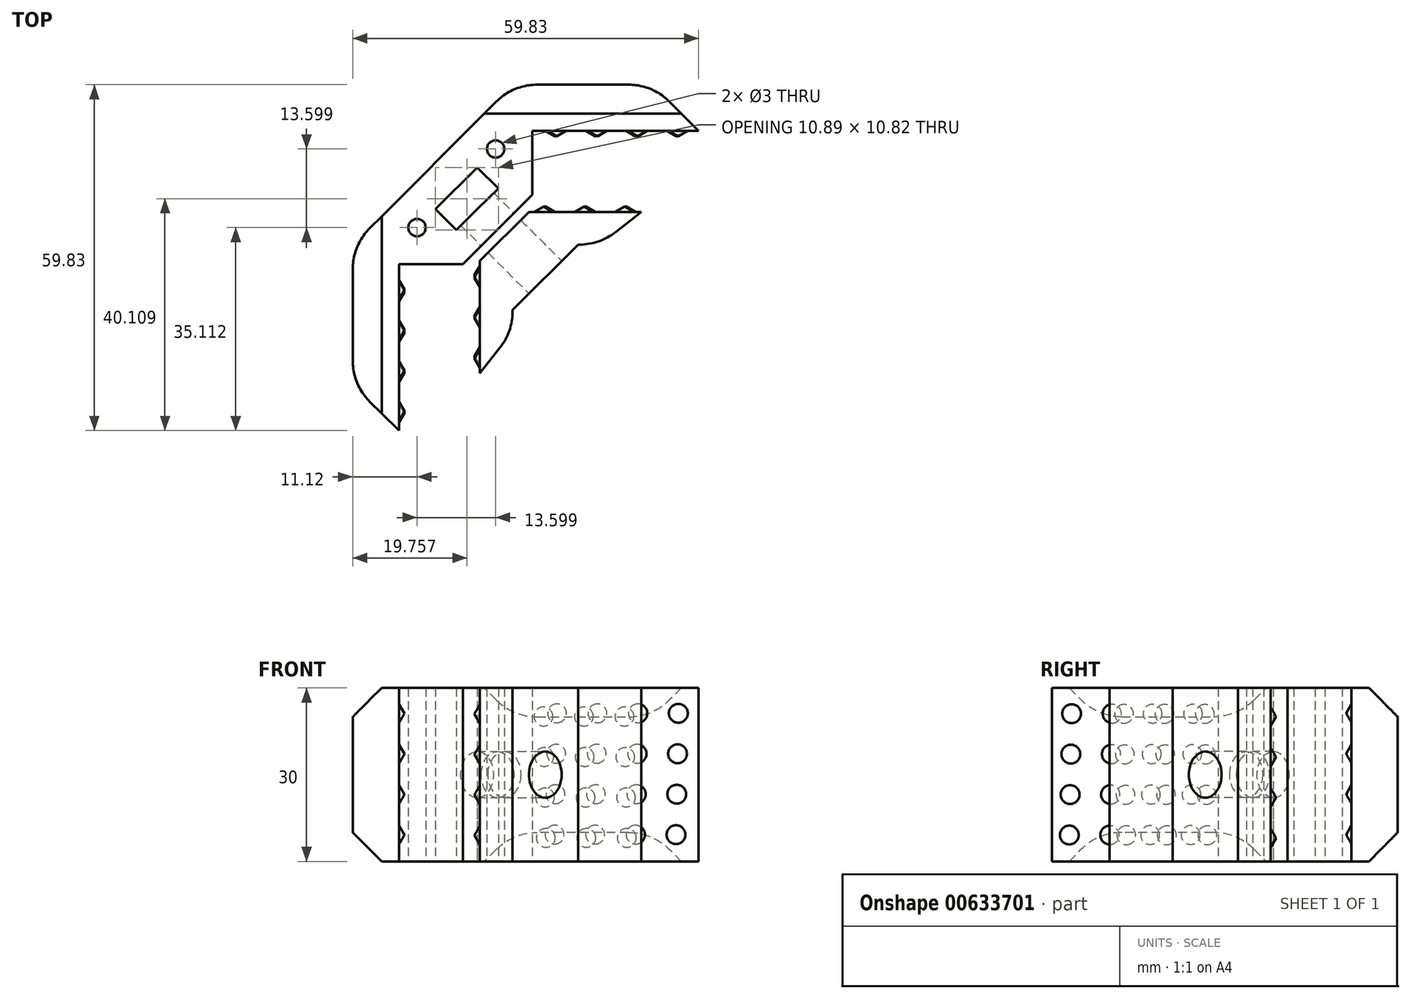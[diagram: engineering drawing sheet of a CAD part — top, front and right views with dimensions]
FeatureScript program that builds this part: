
annotation { "Feature Type Name" : "Feature", "Feature Type Description" : "" }
export const myFeature = defineFeature(function(context is Context, id is Id, definition is map)
    precondition{}
    {
        {
            var Q0;
            Q0=qCreatedBy(makeId("Top.planeOp"),FACE);
            var sketch = newSketch(context, id + "F0", { "sketchPlane" : qUnion([Q0])});
            skLineSegment(sketch, "E0.bottom", {"start": v(0, 0) * mm, "end": v(11.05, 0) * mm});
            skLineSegment(sketch, "E0.left", {"start": v(0, 0) * mm, "end": v(0, -28.76) * mm});
            skLineSegment(sketch, "E0.right", {"start": v(16, -1.41) * mm, "end": v(16, -20.83) * mm});
            skLineSegment(sketch, "E1", {"start": v(23.07, 12.02) * mm, "end": v(23.07, 23.07) * mm});
            skLineSegment(sketch, "E2", {"start": v(23.07, 23.07) * mm, "end": v(51.83, 23.07) * mm});
            skLineSegment(sketch, "E3", {"start": v(24.49, 7.07) * mm, "end": v(43.9, 7.07) * mm});
            skLineSegment(sketch, "E4", {"start": v(0, 0) * mm, "end": v(23.07, 23.07) * mm, "construction": true});
            skLineSegment(sketch, "E5.0", {"start": v(-8, 3.31) * mm, "end": v(-8, -20.83) * mm});
            skLineSegment(sketch, "E5.1", {"start": v(-8, 3.31) * mm, "end": v(19.76, 31.07) * mm});
            skLineSegment(sketch, "E5.2", {"start": v(19.76, 31.07) * mm, "end": v(43.9, 31.07) * mm});
            skLineSegment(sketch, "E6", {"start": v(21.66, -5.66) * mm, "end": v(21.66, -13.66) * mm});
            skLineSegment(sketch, "E7.MirrorCS", {"start": v(28.73, 1.41) * mm, "end": v(36.73, 1.41) * mm});
            skLineSegment(sketch, "E8", {"start": v(21.66, -13.66) * mm, "end": v(16, -20.83) * mm});
            skLineSegment(sketch, "E9", {"start": v(-8, -20.83) * mm, "end": v(0, -28.76) * mm});
            skLineSegment(sketch, "E10.MirrorCS", {"start": v(36.73, 1.41) * mm, "end": v(43.9, 7.07) * mm});
            skLineSegment(sketch, "E11.MirrorCS", {"start": v(43.9, 31.07) * mm, "end": v(51.83, 23.07) * mm});
            skLineSegment(sketch, "E12", {"start": v(9.92, 5.94) * mm, "end": v(6.31, 9.55) * mm});
            skLineSegment(sketch, "E13", {"start": v(6.31, 9.55) * mm, "end": v(13.53, 16.76) * mm});
            skLineSegment(sketch, "E14", {"start": v(13.53, 16.76) * mm, "end": v(17.2, 13.08) * mm});
            skLineSegment(sketch, "E15", {"start": v(17.2, 13.08) * mm, "end": v(13.53, 9.55) * mm});
            skCircle(sketch, "E16", {"center": v(3.12, 6.35) * mm, "radius": 1.5 * mm});
            skLineSegment(sketch, "E17", {"start": v(9.92, 5.94) * mm, "end": v(13.53, 9.55) * mm});
            skCircle(sketch, "E18.MirrorC", {"center": v(16.72, 19.95) * mm, "radius": 1.5 * mm});
            skPoint(sketch, "E19.end.orphan", {"position": v(123.07, 23.07) * mm});
            skPoint(sketch, "E19.start.orphan", {"position": v(123.07, 7.07) * mm});
            skLineSegment(sketch, "E20.0", {"start": v(21.66, -9.9) * mm, "end": v(32.97, 1.41) * mm});
            skLineSegment(sketch, "E21.0", {"start": v(16, -1.41) * mm, "end": v(24.49, 7.07) * mm});
            skLineSegment(sketch, "E22.0", {"start": v(11.05, 0) * mm, "end": v(23.07, 12.02) * mm});
            skPoint(sketch, "E23.orphan", {"position": v(23.07, 7.07) * mm});
            skSolve(sketch);
        }
        {
            var Q0;
            {var subQ7=sQuery(id+"F0.wireOp",EDGE,"E0.bottom");Q0=makeQuery(id+"F0.imprint","IMPRINT",FACE,{"disambiguationData":[TD([[makeQuery(id+"F0.imprint","IMPRINT",EDGE,{"derivedFrom":subQ7}),1.0]])]});}
            extrude(context, id + "F1", {"entities" : qUnion([Q0]), "depth" : 30 * mm, "offsetDistance" : 25 * mm});
        }
        {
            var Q0;
            Q0=makeQuery(id+"F0.imprint","IMPRINT",FACE,{"disambiguationData":[TD([[makeQuery(id+"F0.imprint","IMPRINT",EDGE,{"derivedFrom":sQuery(id+"F0.wireOp",EDGE,"E0.right")}),1.0]])]});
            extrude(context, id + "F2", {"entities" : qUnion([Q0]), "depth" : 30 * mm, "offsetDistance" : 25 * mm});
        }
        {
            var Q0;
            Q0=makeQuery(id+"F2.opExtrude","SWEPT_FACE",FACE,{"disambiguationData":[OSD([sQuery(id+"F0.wireOp",EDGE,"E20.0")])]});
            var sketch = newSketch(context, id + "F3", { "sketchPlane" : qUnion([Q0])});
            skPoint(sketch, "E24", {"position": v(16.31, 15) * mm});
            skPoint(sketch, "E24.positionSnap0", {"position": v(11.31, 15) * mm});
            skPoint(sketch, "E24.positionSnap1", {"position": v(16.31, 30) * mm});
            skCircle(sketch, "E25", {"center": v(16.31, 15) * mm, "radius": 4 * mm});
            skSolve(sketch);
        }
        {
            var Q0;
            Q0=makeQuery(id+"F3.imprint","IMPRINT",FACE,{"disambiguationData":[TD([[makeQuery(id+"F3.imprint","IMPRINT",EDGE,{"derivedFrom":sQuery(id+"F3.wireOp",EDGE,"E25")}),1.0]])]});
            extrude(context, id + "F4", {"entities" : qUnion([Q0]), "operationType" : NewBodyOperationType.REMOVE, "oppositeDirection" : true, "depth" : 23.8 * mm, "offsetDistance" : 25 * mm});
        }
        {
            var Q0;
            Q0=makeQuery(id+"F1.opExtrude","CAP_EDGE",EDGE,{"disambiguationData":[OSD([sQuery(id+"F0.wireOp",EDGE,"E5.0")])],"isStart":false});
            var Q1;
            Q1=makeQuery(id+"F1.opExtrude","CAP_EDGE",EDGE,{"disambiguationData":[OSD([sQuery(id+"F0.wireOp",EDGE,"E5.2")])],"isStart":false});
            var Q2;
            Q2=makeQuery(id+"F1.opExtrude","CAP_EDGE",EDGE,{"disambiguationData":[OSD([sQuery(id+"F0.wireOp",EDGE,"E5.0")])],"isStart":true});
            var Q3;
            Q3=makeQuery(id+"F1.opExtrude","CAP_EDGE",EDGE,{"disambiguationData":[OSD([sQuery(id+"F0.wireOp",EDGE,"E5.2")])],"isStart":true});
            chamfer(context, id + "F5", {"entities" : qUnion([Q0, Q1, Q2, Q3]), "width" : 5 * mm, "tangentPropagation" : true});
        }
        {
            var Q0;
            Q0=makeQuery(id+"F1.opExtrude","SWEPT_EDGE",EDGE,{"disambiguationData":[OSD([sQuery(id+"F0.wireOp",EDGE,"E5.0"),sQuery(id+"F0.wireOp",EDGE,"E9")])]});
            var Q1;
            Q1=makeQuery(id+"F1.opExtrude","SWEPT_EDGE",EDGE,{"disambiguationData":[OSD([sQuery(id+"F0.wireOp",EDGE,"E5.0"),sQuery(id+"F0.wireOp",EDGE,"E5.1")])]});
            var Q2;
            Q2=makeQuery(id+"F1.opExtrude","SWEPT_EDGE",EDGE,{"disambiguationData":[OSD([sQuery(id+"F0.wireOp",EDGE,"E5.1"),sQuery(id+"F0.wireOp",EDGE,"E5.2")])]});
            var Q3;
            Q3=makeQuery(id+"F1.opExtrude","SWEPT_EDGE",EDGE,{"disambiguationData":[OSD([sQuery(id+"F0.wireOp",EDGE,"E5.2"),sQuery(id+"F0.wireOp",EDGE,"E11.MirrorCS")])]});
            var Q4;
            Q4=makeQuery(id+"F2.opExtrude","SWEPT_EDGE",EDGE,{"disambiguationData":[OSD([sQuery(id+"F0.wireOp",EDGE,"E6"),sQuery(id+"F0.wireOp",EDGE,"E8")])]});
            var Q5;
            Q5=makeQuery(id+"F2.opExtrude","SWEPT_EDGE",EDGE,{"disambiguationData":[OSD([sQuery(id+"F0.wireOp",EDGE,"E7.MirrorCS"),sQuery(id+"F0.wireOp",EDGE,"E10.MirrorCS")])]});
            fillet(context, id + "F6", {"entities" : qUnion([Q0, Q1, Q2, Q3, Q4, Q5]), "radius" : 10 * mm, "tangentPropagation" : true, "allowEdgeOverflow" : false});
        }
        {
            var Q0;
            Q0=makeQuery(id+"F1.opExtrude","SWEPT_FACE",FACE,{"disambiguationData":[OSD([sQuery(id+"F0.wireOp",EDGE,"E0.left")])]});
            var sketch = newSketch(context, id + "F7", { "sketchPlane" : qUnion([Q0])});
            skCircle(sketch, "E26", {"center": v(-25.36, 25.55) * mm, "radius": 1.63 * mm});
            skCircle(sketch, "E27.0.1.0", {"center": v(-25.5, 18.55) * mm, "radius": 1.63 * mm});
            skCircle(sketch, "E27.0.2.0", {"center": v(-25.63, 11.55) * mm, "radius": 1.63 * mm});
            skCircle(sketch, "E27.0.3.0", {"center": v(-25.77, 4.55) * mm, "radius": 1.63 * mm});
            skCircle(sketch, "E27.1.0.0", {"center": v(-18.36, 25.55) * mm, "radius": 1.63 * mm});
            skCircle(sketch, "E27.1.1.0", {"center": v(-18.5, 18.55) * mm, "radius": 1.63 * mm});
            skCircle(sketch, "E27.1.2.0", {"center": v(-18.63, 11.55) * mm, "radius": 1.63 * mm});
            skCircle(sketch, "E27.1.3.0", {"center": v(-18.77, 4.55) * mm, "radius": 1.63 * mm});
            skCircle(sketch, "E27.2.0.0", {"center": v(-11.36, 25.55) * mm, "radius": 1.63 * mm});
            skCircle(sketch, "E27.2.1.0", {"center": v(-11.5, 18.55) * mm, "radius": 1.63 * mm});
            skCircle(sketch, "E27.2.2.0", {"center": v(-11.63, 11.55) * mm, "radius": 1.63 * mm});
            skCircle(sketch, "E27.2.3.0", {"center": v(-11.77, 4.55) * mm, "radius": 1.63 * mm});
            skCircle(sketch, "E27.3.0.0", {"center": v(-4.36, 25.55) * mm, "radius": 1.63 * mm});
            skCircle(sketch, "E27.3.1.0", {"center": v(-4.5, 18.55) * mm, "radius": 1.63 * mm});
            skCircle(sketch, "E27.3.2.0", {"center": v(-4.63, 11.55) * mm, "radius": 1.63 * mm});
            skCircle(sketch, "E27.3.3.0", {"center": v(-4.77, 4.55) * mm, "radius": 1.63 * mm});
            skLineSegment(sketch, "E27.direction1", {"start": v(-25.36, 25.55) * mm, "end": v(-18.36, 25.55) * mm, "construction": true});
            skLineSegment(sketch, "E27.direction2", {"start": v(-25.36, 25.55) * mm, "end": v(-25.5, 18.55) * mm, "construction": true});
            skSolve(sketch);
        }
        {
            var Q0;
            Q0=makeQuery(id+"F1.opExtrude","SWEPT_FACE",FACE,{"disambiguationData":[OSD([sQuery(id+"F0.wireOp",EDGE,"E2")])]});
            var sketch = newSketch(context, id + "F8", { "sketchPlane" : qUnion([Q0])});
            skCircle(sketch, "E28", {"center": v(27.34, 25.61) * mm, "radius": 1.63 * mm});
            skCircle(sketch, "E29.0.1.0", {"center": v(27.2, 18.61) * mm, "radius": 1.63 * mm});
            skCircle(sketch, "E29.0.2.0", {"center": v(27.07, 11.62) * mm, "radius": 1.63 * mm});
            skCircle(sketch, "E29.0.3.0", {"center": v(26.93, 4.62) * mm, "radius": 1.63 * mm});
            skCircle(sketch, "E29.1.0.0", {"center": v(34.34, 25.61) * mm, "radius": 1.63 * mm});
            skCircle(sketch, "E29.1.1.0", {"center": v(34.2, 18.61) * mm, "radius": 1.63 * mm});
            skCircle(sketch, "E29.1.2.0", {"center": v(34.07, 11.62) * mm, "radius": 1.63 * mm});
            skCircle(sketch, "E29.1.3.0", {"center": v(33.93, 4.62) * mm, "radius": 1.63 * mm});
            skCircle(sketch, "E29.2.0.0", {"center": v(41.34, 25.61) * mm, "radius": 1.63 * mm});
            skCircle(sketch, "E29.2.1.0", {"center": v(41.2, 18.61) * mm, "radius": 1.63 * mm});
            skCircle(sketch, "E29.2.2.0", {"center": v(41.07, 11.62) * mm, "radius": 1.63 * mm});
            skCircle(sketch, "E29.2.3.0", {"center": v(40.93, 4.62) * mm, "radius": 1.63 * mm});
            skCircle(sketch, "E29.3.0.0", {"center": v(48.34, 25.61) * mm, "radius": 1.63 * mm});
            skCircle(sketch, "E29.3.1.0", {"center": v(48.2, 18.61) * mm, "radius": 1.63 * mm});
            skCircle(sketch, "E29.3.2.0", {"center": v(48.07, 11.62) * mm, "radius": 1.63 * mm});
            skCircle(sketch, "E29.3.3.0", {"center": v(47.93, 4.62) * mm, "radius": 1.63 * mm});
            skLineSegment(sketch, "E29.direction1", {"start": v(27.34, 25.61) * mm, "end": v(34.34, 25.61) * mm, "construction": true});
            skLineSegment(sketch, "E29.direction2", {"start": v(27.34, 25.61) * mm, "end": v(27.2, 18.61) * mm, "construction": true});
            skSolve(sketch);
        }
        {
            var Q0;
            Q0=makeQuery(id+"F7.imprint","IMPRINT",FACE,{"disambiguationData":[TD([[makeQuery(id+"F7.imprint","IMPRINT",EDGE,{"derivedFrom":sQuery(id+"F7.wireOp",EDGE,"E27.0.1.0")}),1.0]])]});
            var Q1;
            Q1=makeQuery(id+"F7.imprint","IMPRINT",FACE,{"disambiguationData":[TD([[makeQuery(id+"F7.imprint","IMPRINT",EDGE,{"derivedFrom":sQuery(id+"F7.wireOp",EDGE,"E27.0.2.0")}),1.0]])]});
            var Q2;
            Q2=makeQuery(id+"F7.imprint","IMPRINT",FACE,{"disambiguationData":[TD([[makeQuery(id+"F7.imprint","IMPRINT",EDGE,{"derivedFrom":sQuery(id+"F7.wireOp",EDGE,"E27.0.3.0")}),1.0]])]});
            var Q3;
            Q3=makeQuery(id+"F7.imprint","IMPRINT",FACE,{"disambiguationData":[TD([[makeQuery(id+"F7.imprint","IMPRINT",EDGE,{"derivedFrom":sQuery(id+"F7.wireOp",EDGE,"E27.1.3.0")}),1.0]])]});
            var Q4;
            Q4=makeQuery(id+"F7.imprint","IMPRINT",FACE,{"disambiguationData":[TD([[makeQuery(id+"F7.imprint","IMPRINT",EDGE,{"derivedFrom":sQuery(id+"F7.wireOp",EDGE,"E27.2.3.0")}),1.0]])]});
            var Q5;
            Q5=makeQuery(id+"F7.imprint","IMPRINT",FACE,{"disambiguationData":[TD([[makeQuery(id+"F7.imprint","IMPRINT",EDGE,{"derivedFrom":sQuery(id+"F7.wireOp",EDGE,"E27.3.3.0")}),1.0]])]});
            var Q6;
            Q6=makeQuery(id+"F7.imprint","IMPRINT",FACE,{"disambiguationData":[TD([[makeQuery(id+"F7.imprint","IMPRINT",EDGE,{"derivedFrom":sQuery(id+"F7.wireOp",EDGE,"E27.2.2.0")}),1.0]])]});
            var Q7;
            Q7=makeQuery(id+"F7.imprint","IMPRINT",FACE,{"disambiguationData":[TD([[makeQuery(id+"F7.imprint","IMPRINT",EDGE,{"derivedFrom":sQuery(id+"F7.wireOp",EDGE,"E27.1.2.0")}),1.0]])]});
            var Q8;
            Q8=makeQuery(id+"F7.imprint","IMPRINT",FACE,{"disambiguationData":[TD([[makeQuery(id+"F7.imprint","IMPRINT",EDGE,{"derivedFrom":sQuery(id+"F7.wireOp",EDGE,"E27.2.1.0")}),1.0]])]});
            var Q9;
            Q9=makeQuery(id+"F7.imprint","IMPRINT",FACE,{"disambiguationData":[TD([[makeQuery(id+"F7.imprint","IMPRINT",EDGE,{"derivedFrom":sQuery(id+"F7.wireOp",EDGE,"E27.3.1.0")}),1.0]])]});
            var Q10;
            Q10=makeQuery(id+"F7.imprint","IMPRINT",FACE,{"disambiguationData":[TD([[makeQuery(id+"F7.imprint","IMPRINT",EDGE,{"derivedFrom":sQuery(id+"F7.wireOp",EDGE,"E27.3.0.0")}),1.0]])]});
            var Q11;
            Q11=makeQuery(id+"F7.imprint","IMPRINT",FACE,{"disambiguationData":[TD([[makeQuery(id+"F7.imprint","IMPRINT",EDGE,{"derivedFrom":sQuery(id+"F7.wireOp",EDGE,"E27.3.2.0")}),1.0]])]});
            var Q12;
            Q12=makeQuery(id+"F7.imprint","IMPRINT",FACE,{"disambiguationData":[TD([[makeQuery(id+"F7.imprint","IMPRINT",EDGE,{"derivedFrom":sQuery(id+"F7.wireOp",EDGE,"E27.2.0.0")}),1.0]])]});
            var Q13;
            Q13=makeQuery(id+"F7.imprint","IMPRINT",FACE,{"disambiguationData":[TD([[makeQuery(id+"F7.imprint","IMPRINT",EDGE,{"derivedFrom":sQuery(id+"F7.wireOp",EDGE,"E27.1.0.0")}),1.0]])]});
            var Q14;
            Q14=makeQuery(id+"F7.imprint","IMPRINT",FACE,{"disambiguationData":[TD([[makeQuery(id+"F7.imprint","IMPRINT",EDGE,{"derivedFrom":sQuery(id+"F7.wireOp",EDGE,"E26")}),1.0]])]});
            var Q15;
            Q15=makeQuery(id+"F7.imprint","IMPRINT",FACE,{"disambiguationData":[TD([[makeQuery(id+"F7.imprint","IMPRINT",EDGE,{"derivedFrom":sQuery(id+"F7.wireOp",EDGE,"E27.1.1.0")}),1.0]])]});
            extrude(context, id + "F9", {"entities" : qUnion([Q0, Q1, Q2, Q3, Q4, Q5, Q6, Q7, Q8, Q9, Q10, Q11, Q12, Q13, Q14, Q15]), "operationType" : NewBodyOperationType.ADD, "depth" : 1 * mm, "offsetDistance" : 25 * mm, "hasDraft" : true, "draftAngle" : 60 * degree, "draftPullDirection" : true});
        }
        {
            var Q0;
            Q0 = qSketchRegion(id + "F8", true);
            extrude(context, id + "F10", {"entities" : qUnion([Q0]), "operationType" : NewBodyOperationType.ADD, "depth" : 1 * mm, "offsetDistance" : 25 * mm, "hasDraft" : true, "draftAngle" : 60 * degree, "draftPullDirection" : true});
        }
        {
            var Q0;
            Q0=makeQuery(id+"F2.opExtrude","SWEPT_FACE",FACE,{"disambiguationData":[OSD([sQuery(id+"F0.wireOp",EDGE,"E0.right")])]});
            var sketch = newSketch(context, id + "F11", { "sketchPlane" : qUnion([Q0])});
            skCircle(sketch, "E30", {"center": v(4.3, 25.51) * mm, "radius": 1.63 * mm});
            skCircle(sketch, "E31.0.1.0", {"center": v(4.16, 18.51) * mm, "radius": 1.63 * mm});
            skCircle(sketch, "E31.0.2.0", {"center": v(4.03, 11.51) * mm, "radius": 1.63 * mm});
            skCircle(sketch, "E31.0.3.0", {"center": v(3.9, 4.52) * mm, "radius": 1.63 * mm});
            skCircle(sketch, "E31.1.0.0", {"center": v(11.3, 25.51) * mm, "radius": 1.63 * mm});
            skCircle(sketch, "E31.1.1.0", {"center": v(11.16, 18.51) * mm, "radius": 1.63 * mm});
            skCircle(sketch, "E31.1.2.0", {"center": v(11.03, 11.51) * mm, "radius": 1.63 * mm});
            skCircle(sketch, "E31.1.3.0", {"center": v(10.9, 4.52) * mm, "radius": 1.63 * mm});
            skCircle(sketch, "E31.2.0.0", {"center": v(18.3, 25.51) * mm, "radius": 1.63 * mm});
            skCircle(sketch, "E31.2.1.0", {"center": v(18.16, 18.51) * mm, "radius": 1.63 * mm});
            skCircle(sketch, "E31.2.2.0", {"center": v(18.03, 11.51) * mm, "radius": 1.63 * mm});
            skCircle(sketch, "E31.2.3.0", {"center": v(17.9, 4.52) * mm, "radius": 1.63 * mm});
            skLineSegment(sketch, "E31.direction1", {"start": v(4.3, 25.51) * mm, "end": v(11.3, 25.51) * mm, "construction": true});
            skLineSegment(sketch, "E31.direction2", {"start": v(4.3, 25.51) * mm, "end": v(4.16, 18.51) * mm, "construction": true});
            skSolve(sketch);
        }
        {
            var Q0;
            Q0 = qSketchRegion(id + "F11", true);
            extrude(context, id + "F12", {"entities" : qUnion([Q0]), "operationType" : NewBodyOperationType.ADD, "depth" : 1 * mm, "offsetDistance" : 25 * mm, "hasDraft" : true, "draftAngle" : 60 * degree, "draftPullDirection" : true});
        }
        {
            var Q0;
            Q0=makeQuery(id+"F2.opExtrude","SWEPT_FACE",FACE,{"disambiguationData":[OSD([sQuery(id+"F0.wireOp",EDGE,"E3")])]});
            var sketch = newSketch(context, id + "F13", { "sketchPlane" : qUnion([Q0])});
            skCircle(sketch, "E32.1.0.0", {"center": v(-41, 25.06) * mm, "radius": 1.63 * mm});
            skCircle(sketch, "E32.1.1.0", {"center": v(-41.14, 18.06) * mm, "radius": 1.63 * mm});
            skCircle(sketch, "E32.1.2.0", {"center": v(-41.27, 11.06) * mm, "radius": 1.63 * mm});
            skCircle(sketch, "E32.1.3.0", {"center": v(-41.4, 4.06) * mm, "radius": 1.63 * mm});
            skCircle(sketch, "E32.2.0.0", {"center": v(-34, 25.06) * mm, "radius": 1.63 * mm});
            skCircle(sketch, "E32.2.1.0", {"center": v(-34.14, 18.06) * mm, "radius": 1.63 * mm});
            skCircle(sketch, "E32.2.2.0", {"center": v(-34.27, 11.06) * mm, "radius": 1.63 * mm});
            skCircle(sketch, "E32.2.3.0", {"center": v(-34.4, 4.06) * mm, "radius": 1.63 * mm});
            skCircle(sketch, "E32.3.0.0", {"center": v(-27, 25.06) * mm, "radius": 1.63 * mm});
            skCircle(sketch, "E32.3.1.0", {"center": v(-27.14, 18.06) * mm, "radius": 1.63 * mm});
            skCircle(sketch, "E32.3.2.0", {"center": v(-27.27, 11.06) * mm, "radius": 1.63 * mm});
            skCircle(sketch, "E32.3.3.0", {"center": v(-27.4, 4.06) * mm, "radius": 1.63 * mm});
            skLineSegment(sketch, "E32.direction1", {"start": v(-48, 25.06) * mm, "end": v(-41, 25.06) * mm, "construction": true});
            skLineSegment(sketch, "E32.direction2", {"start": v(-48, 25.06) * mm, "end": v(-48.14, 18.06) * mm, "construction": true});
            skSolve(sketch);
        }
        {
            var Q0;
            Q0 = qSketchRegion(id + "F13", true);
            extrude(context, id + "F14", {"entities" : qUnion([Q0]), "operationType" : NewBodyOperationType.ADD, "depth" : 1 * mm, "offsetDistance" : 25 * mm, "hasDraft" : true, "draftAngle" : 60 * degree, "draftPullDirection" : true});
        }
        {
            var Q0;
            Q0=makeQuery(id+"F2.opExtrude","SWEPT_BODY",BODY,{"disambiguationData":[OSD([sQuery(id+"F0.wireOp",EDGE,"E0.right"),sQuery(id+"F0.wireOp",EDGE,"E3"),sQuery(id+"F0.wireOp",EDGE,"E6"),sQuery(id+"F0.wireOp",EDGE,"E7.MirrorCS"),sQuery(id+"F0.wireOp",EDGE,"E8"),sQuery(id+"F0.wireOp",EDGE,"E10.MirrorCS"),sQuery(id+"F0.wireOp",EDGE,"E20.0"),sQuery(id+"F0.wireOp",EDGE,"E21.0")])]});
            transform(context, id + "F15", {"entities" : qUnion([Q0]), "transformType" : TransformType.TRANSLATION_3D, "dx" : -2 * mm, "dy" : 2 * mm, "dz" : 0 * mm, "makeCopy" : false});
        }
    });
